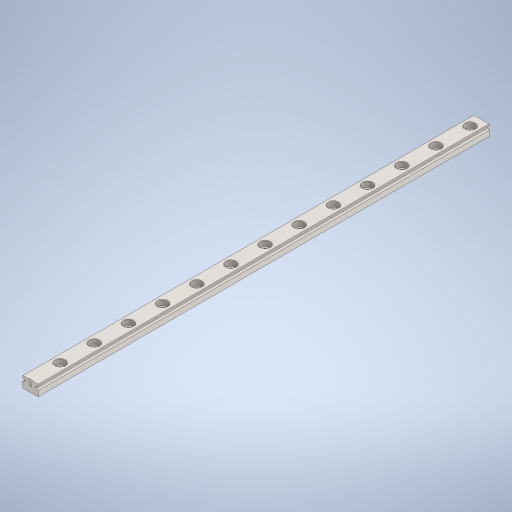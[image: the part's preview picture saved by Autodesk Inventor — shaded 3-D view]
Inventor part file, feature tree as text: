
AUTODESK INVENTOR PART (.ipt)
format: ipt  version: 2024.2 (Build 282272000, 272)  size: 339,456 bytes
history: native  units: mm
features: other x2, extrude x1, sketch x1
ambient origin geometry x8: Origin, YZ Plane, XZ Plane, XY Plane, X Axis, Y Axis, Z Axis, Center Point
bodies: Body1 (feature_tree)
feature tree (4):
  other  "Твердое тело1"
  extrude  "Выдавливание1"  Depth=52.0mm TaperAngle=0.0deg
  sketch  "Эскиз1"
  other  "LPattern1"
